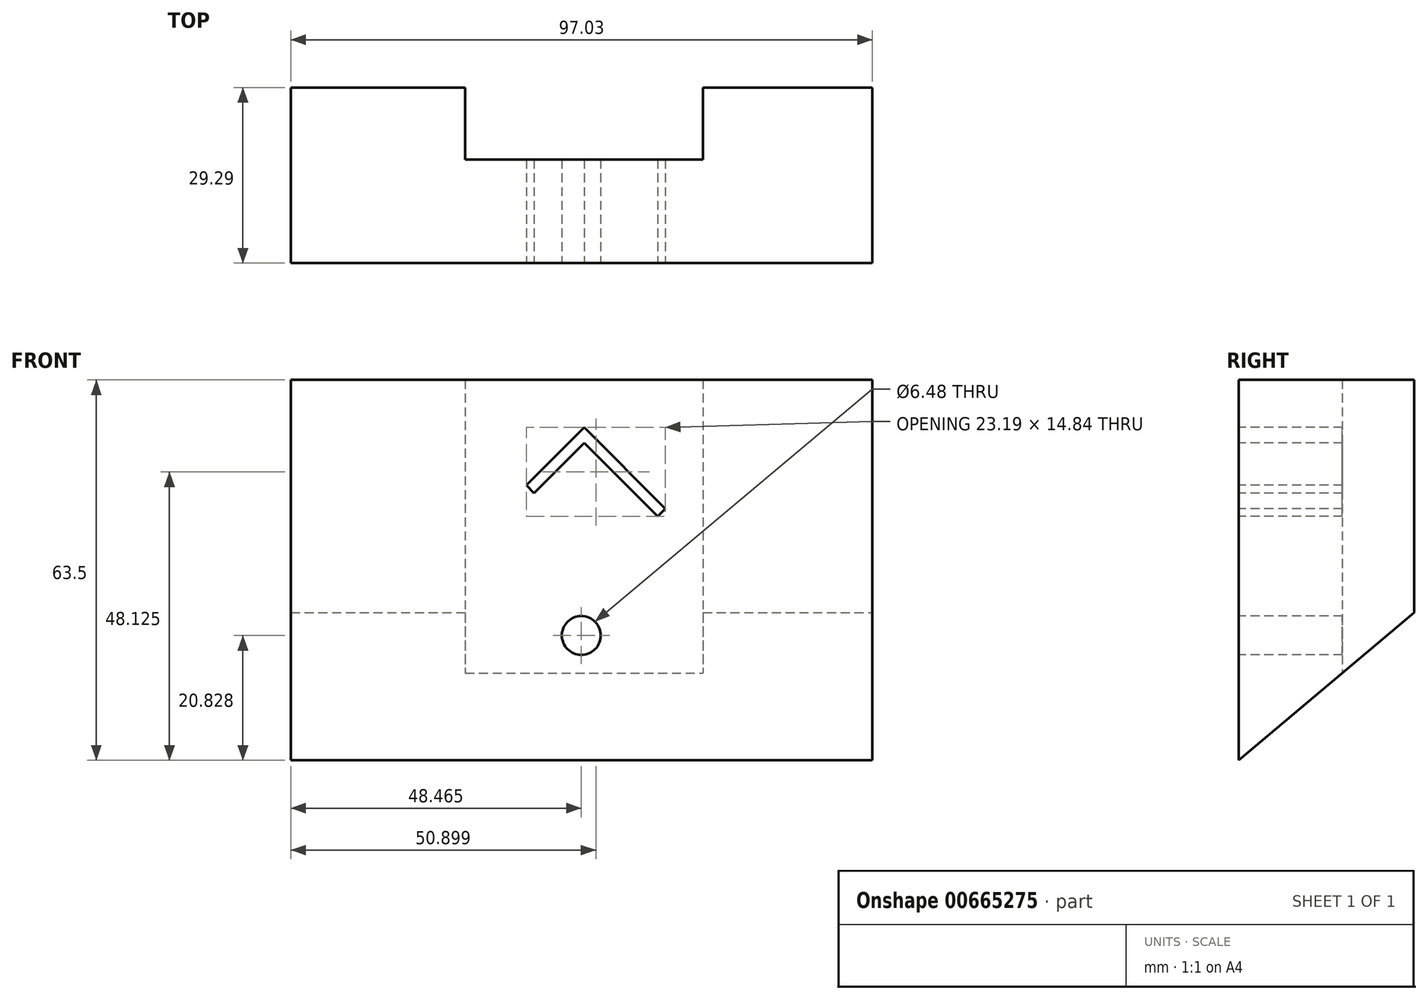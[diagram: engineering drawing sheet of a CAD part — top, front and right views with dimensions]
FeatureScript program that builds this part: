
annotation { "Feature Type Name" : "Feature", "Feature Type Description" : "" }
export const myFeature = defineFeature(function(context is Context, id is Id, definition is map)
    precondition{}
    {
        {
            var Q0;
            Q0=qCreatedBy(makeId("Top.planeOp"),FACE);
            var sketch = newSketch(context, id + "F0", { "sketchPlane" : qUnion([Q0])});
            skLineSegment(sketch, "E0.bottom", {"start": v(-45.16, 14.5) * mm, "end": v(51.87, 14.5) * mm});
            skLineSegment(sketch, "E0.top", {"start": v(-45.16, -14.78) * mm, "end": v(51.87, -14.78) * mm});
            skLineSegment(sketch, "E0.left", {"start": v(-45.16, 14.5) * mm, "end": v(-45.16, -14.78) * mm});
            skLineSegment(sketch, "E0.right", {"start": v(51.87, 14.5) * mm, "end": v(51.87, -14.78) * mm});
            skSolve(sketch);
        }
        {
            var Q0;
            Q0=makeQuery(id+"F0.imprint","IMPRINT",FACE,{"disambiguationData":[TD([[makeQuery(id+"F0.imprint","IMPRINT",EDGE,{"derivedFrom":sQuery(id+"F0.wireOp",EDGE,"E0.bottom")}),-1.0]])]});
            var sketch = newSketch(context, id + "F1", { "sketchPlane" : qUnion([Q0])});
            skLineSegment(sketch, "E1.bottom", {"start": v(-16.06, 14.5) * mm, "end": v(23.61, 14.5) * mm});
            skLineSegment(sketch, "E1.top", {"start": v(-16.06, 2.5) * mm, "end": v(23.61, 2.5) * mm});
            skLineSegment(sketch, "E1.left", {"start": v(-16.06, 14.5) * mm, "end": v(-16.06, 2.5) * mm});
            skLineSegment(sketch, "E1.right", {"start": v(23.61, 14.5) * mm, "end": v(23.61, 2.5) * mm});
            skSolve(sketch);
        }
        {
            var Q0;
            Q0 = qSketchRegion(id + "F0", true);
            extrude(context, id + "F2", {"entities" : qUnion([Q0]), "depth" : 63.5 * mm, "offsetDistance" : 25.4 * mm});
        }
        {
            var Q0;
            Q0 = qSketchRegion(id + "F1", true);
            extrude(context, id + "F3", {"entities" : qUnion([Q0]), "operationType" : NewBodyOperationType.REMOVE, "depth" : 63.5 * mm, "offsetDistance" : 25.4 * mm});
        }
        {
            var Q0;
            Q0=makeQuery(id+"F2.opExtrude","SWEPT_FACE",FACE,{"disambiguationData":[OSD([sQuery(id+"F0.wireOp",EDGE,"E0.right")])]});
            var sketch = newSketch(context, id + "F4", { "sketchPlane" : qUnion([Q0])});
            skLineSegment(sketch, "E2", {"start": v(14.5, 24.64) * mm, "end": v(-14.78, 0) * mm});
            skLineSegment(sketch, "E3", {"start": v(-14.78, 0) * mm, "end": v(14.5, 0) * mm});
            skLineSegment(sketch, "E4", {"start": v(14.5, 0) * mm, "end": v(14.5, 24.64) * mm});
            skSolve(sketch);
        }
        {
            var Q0;
            Q0 = qSketchRegion(id + "F4", true);
            extrude(context, id + "F5", {"entities" : qUnion([Q0]), "operationType" : NewBodyOperationType.REMOVE, "oppositeDirection" : true, "depth" : 97.03 * mm, "offsetDistance" : 25.4 * mm});
        }
        {
            var Q0;
            Q0=makeQuery(id+"F2.opExtrude","SWEPT_FACE",FACE,{"disambiguationData":[OSD([sQuery(id+"F0.wireOp",EDGE,"E0.top")])]});
            var sketch = newSketch(context, id + "F6", { "sketchPlane" : qUnion([Q0])});
            skCircle(sketch, "E5", {"center": v(3.3, 20.83) * mm, "radius": 3.24 * mm});
            skSolve(sketch);
        }
        {
            var Q0;
            Q0 = qSketchRegion(id + "F6", true);
            extrude(context, id + "F7", {"entities" : qUnion([Q0]), "operationType" : NewBodyOperationType.REMOVE, "oppositeDirection" : true, "depth" : 25.4 * mm, "offsetDistance" : 25.4 * mm});
        }
        {
            var Q0;
            Q0=makeQuery(id+"F2.opExtrude","SWEPT_FACE",FACE,{"disambiguationData":[OSD([sQuery(id+"F0.wireOp",EDGE,"E0.top")])]});
            var sketch = newSketch(context, id + "F8", { "sketchPlane" : qUnion([Q0])});
            skLineSegment(sketch, "E6", {"start": v(3.8, 55.54) * mm, "end": v(17.33, 42) * mm});
            skLineSegment(sketch, "E7", {"start": v(17.33, 42) * mm, "end": v(16.04, 40.7) * mm});
            skLineSegment(sketch, "E8", {"start": v(-5.85, 45.9) * mm, "end": v(-4.56, 44.6) * mm});
            skLineSegment(sketch, "E9", {"start": v(-4.56, 44.6) * mm, "end": v(3.8, 52.96) * mm});
            skLineSegment(sketch, "E10", {"start": v(3.8, 55.54) * mm, "end": v(-5.85, 45.9) * mm});
            skLineSegment(sketch, "E11", {"start": v(3.8, 52.96) * mm, "end": v(16.04, 40.7) * mm});
            skSolve(sketch);
        }
        {
            var Q0;
            Q0 = qSketchRegion(id + "F8", true);
            extrude(context, id + "F9", {"entities" : qUnion([Q0]), "operationType" : NewBodyOperationType.REMOVE, "oppositeDirection" : true, "depth" : 25.4 * mm, "offsetDistance" : 25.4 * mm});
        }
    });
